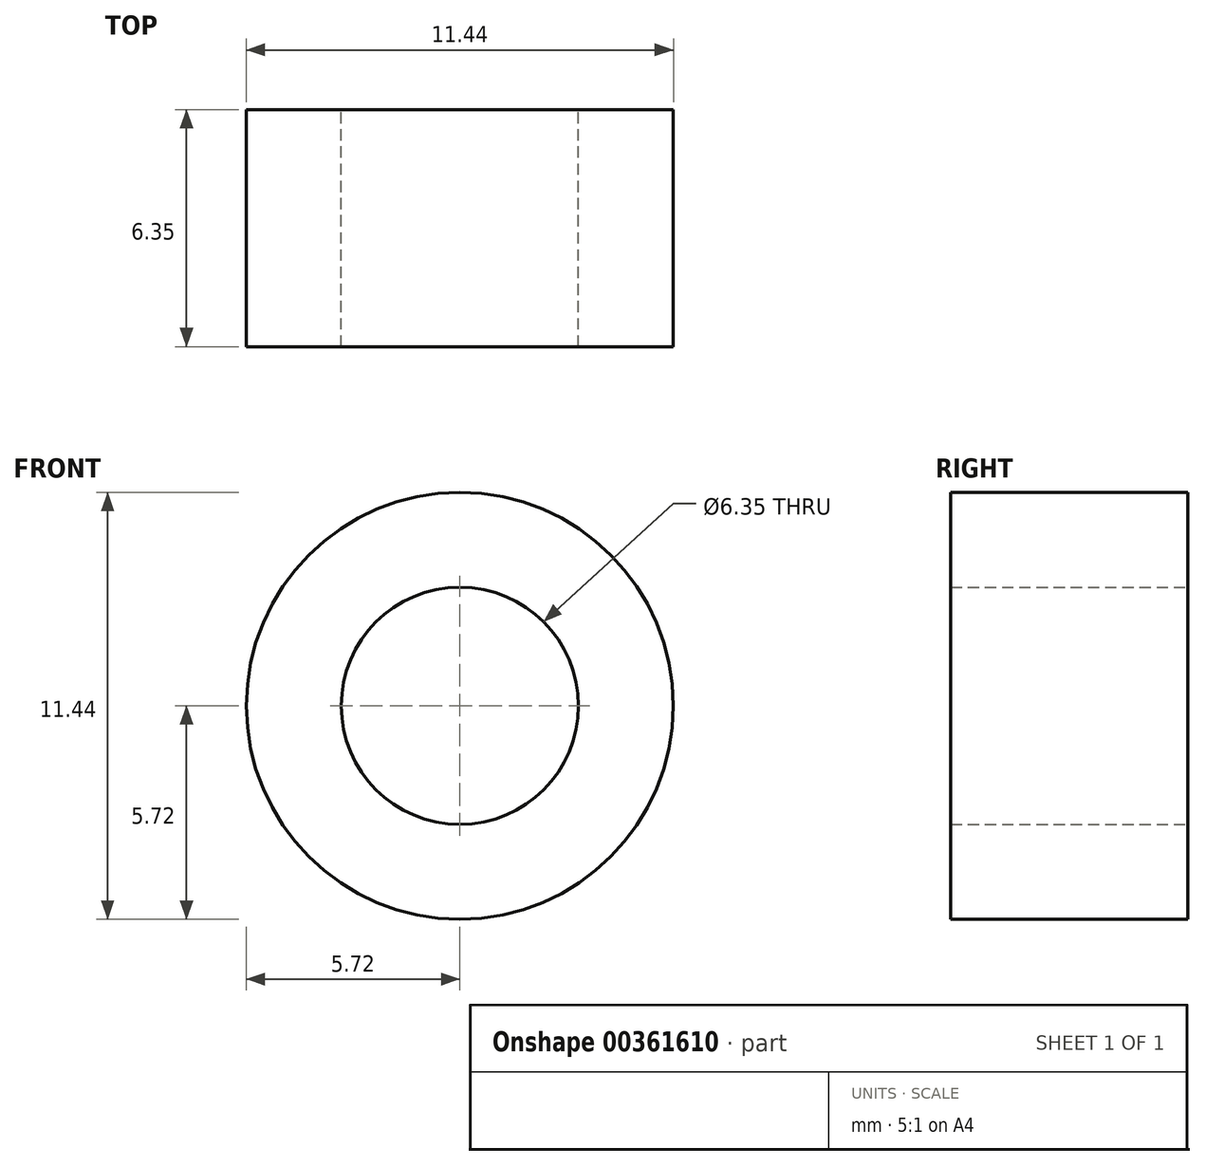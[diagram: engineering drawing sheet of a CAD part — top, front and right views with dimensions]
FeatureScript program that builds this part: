
annotation { "Feature Type Name" : "Feature", "Feature Type Description" : "" }
export const myFeature = defineFeature(function(context is Context, id is Id, definition is map)
    precondition{}
    {
        {
            var Q0;
            Q0=qCreatedBy(makeId("Front.planeOp"),FACE);
            var sketch = newSketch(context, id + "F0", { "sketchPlane" : qUnion([Q0])});
            skCircle(sketch, "E0", {"center": v(0, 0) * mm, "radius": 3.18 * mm});
            skCircle(sketch, "E1", {"center": v(0, 0) * mm, "radius": 5.72 * mm});
            skSolve(sketch);
        }
        {
            var Q0;
            Q0=makeQuery(id+"F0.imprint","IMPRINT",FACE,{"disambiguationData":[TD([[makeQuery(id+"F0.imprint","IMPRINT",EDGE,{"derivedFrom":sQuery(id+"F0.wireOp",EDGE,"E0")}),-1.0]])]});
            extrude(context, id + "F1", {"entities" : qUnion([Q0]), "depth" : 6.35 * mm});
        }
    });
